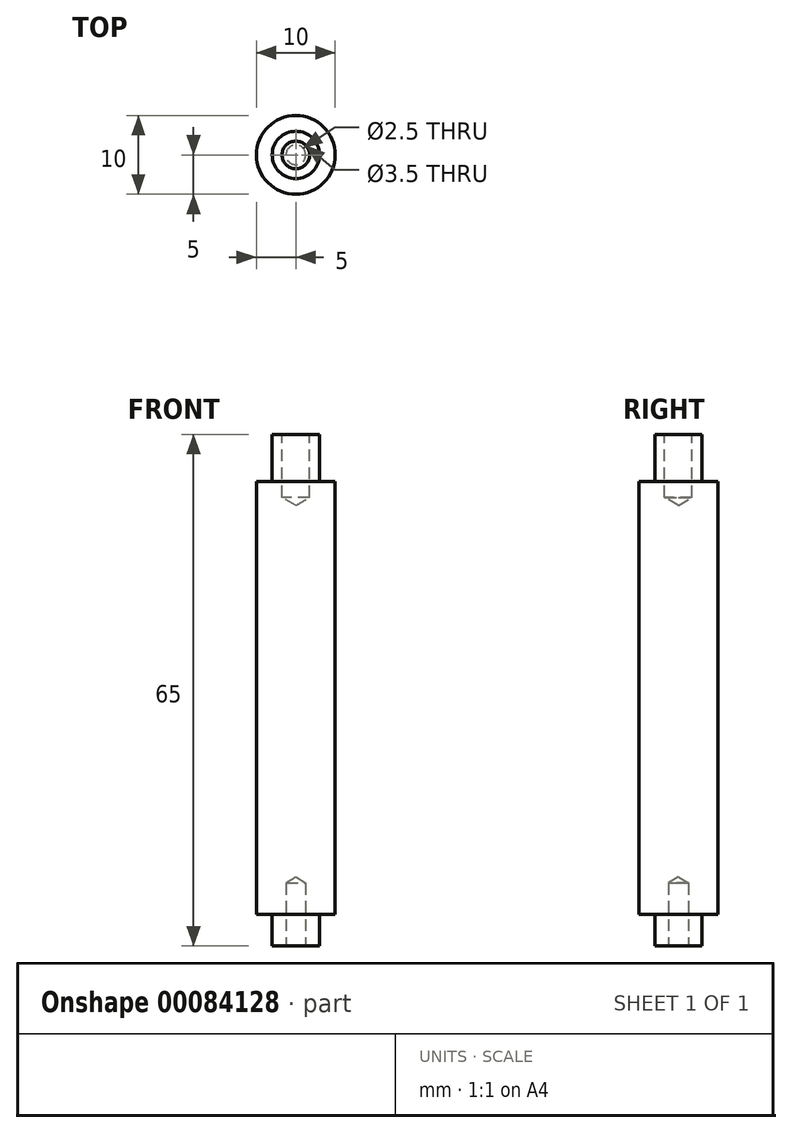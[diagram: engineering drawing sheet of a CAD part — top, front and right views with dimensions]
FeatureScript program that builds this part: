
annotation { "Feature Type Name" : "Feature", "Feature Type Description" : "" }
export const myFeature = defineFeature(function(context is Context, id is Id, definition is map)
    precondition{}
    {
        {
            var Q0;
            Q0=qCreatedBy(makeId("Top.planeOp"),FACE);
            var sketch = newSketch(context, id + "F0", { "sketchPlane" : qUnion([Q0])});
            skCircle(sketch, "E0", {"center": v(0, 0) * mm, "radius": 5 * mm});
            skCircle(sketch, "E1", {"center": v(0, 0) * mm, "radius": 3 * mm});
            skSolve(sketch);
        }
        {
            var Q0;
            Q0=makeQuery(id+"F0.imprint","IMPRINT",FACE,{"disambiguationData":[TD([[makeQuery(id+"F0.imprint","IMPRINT",EDGE,{"derivedFrom":sQuery(id+"F0.wireOp",EDGE,"E1")}),1.0]])]});
            extrude(context, id + "F1", {"entities" : qUnion([Q0]), "depth" : 61 * mm, "hasSecondDirection" : true, "secondDirectionOppositeDirection" : true, "secondDirectionDepth" : 4 * mm});
        }
        {
            var Q0;
            Q0=makeQuery(id+"F0.imprint","IMPRINT",FACE,{"disambiguationData":[TD([[makeQuery(id+"F0.imprint","IMPRINT",EDGE,{"derivedFrom":sQuery(id+"F0.wireOp",EDGE,"E0")}),1.0]])]});
            extrude(context, id + "F2", {"entities" : qUnion([Q0]), "operationType" : NewBodyOperationType.ADD, "depth" : 55 * mm});
        }
        {
            var Q0;
            Q0=makeQuery(id+"F1.opExtrude","CAP_FACE",FACE,{"disambiguationData":[OSD([sQuery(id+"F0.wireOp",EDGE,"E1")])],"isStart":true});
            var sketch = newSketch(context, id + "F3", { "sketchPlane" : qUnion([Q0])});
            skPoint(sketch, "E2", {"position": v(0, 0) * mm});
            skSolve(sketch);
        }
        {
            var Q0;
            Q0=makeQuery(id+"F1.opExtrude","CAP_FACE",FACE,{"disambiguationData":[OSD([sQuery(id+"F0.wireOp",EDGE,"E1")])],"isStart":false});
            var sketch = newSketch(context, id + "F4", { "sketchPlane" : qUnion([Q0])});
            skPoint(sketch, "E3", {"position": v(0, 0) * mm});
            skSolve(sketch);
        }
        {
            var Q0;
            Q0=sQuery(id+"F3.wireOp",VERTEX,"E2");
            var Q1;
            Q1=makeQuery(id+"F1.opExtrude","SWEPT_BODY",BODY,{"disambiguationData":[OSD([sQuery(id+"F0.wireOp",EDGE,"E1")])]});
            hole(context, id + "F5", {"style" : HoleStyle.SIMPLE, "endStyle" : HoleEndStyle.BLIND, "holeDiameter" : 2.5 * mm, "holeDepth" : 8 * mm, "locations" : qUnion([Q0]), "scope" : qUnion([Q1])});
        }
        {
            var Q0;
            Q0=sQuery(id+"F4.wireOp",VERTEX,"E3");
            var Q1;
            Q1=makeQuery(id+"F1.opExtrude","SWEPT_BODY",BODY,{"disambiguationData":[OSD([sQuery(id+"F0.wireOp",EDGE,"E1")])]});
            hole(context, id + "F6", {"style" : HoleStyle.SIMPLE, "endStyle" : HoleEndStyle.BLIND, "holeDiameter" : 3.5 * mm, "holeDepth" : 8 * mm, "locations" : qUnion([Q0]), "scope" : qUnion([Q1])});
        }
    });
